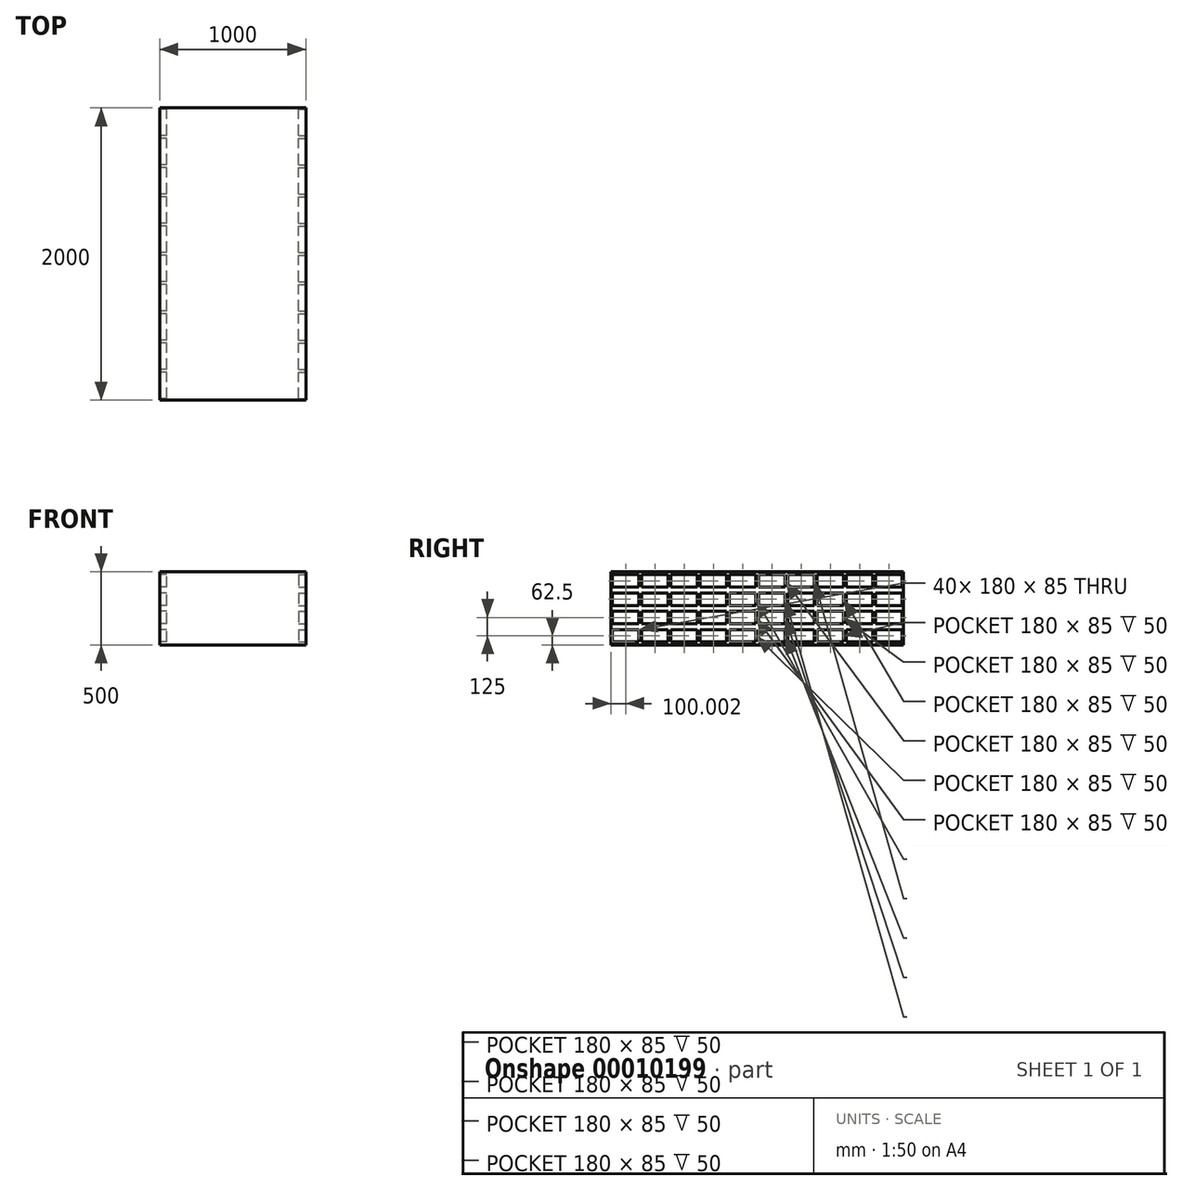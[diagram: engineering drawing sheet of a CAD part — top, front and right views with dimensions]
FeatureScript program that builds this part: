
annotation { "Feature Type Name" : "Feature", "Feature Type Description" : "" }
export const myFeature = defineFeature(function(context is Context, id is Id, definition is map)
    precondition{}
    {
        {
            var Q0;
            Q0=qCreatedBy(makeId("Top.planeOp"),FACE);
            var sketch = newSketch(context, id + "F0", { "sketchPlane" : qUnion([Q0])});
            skLineSegment(sketch, "E0.bottom", {"start": v(-315.45, -1000.92) * mm, "end": v(684.55, -1000.92) * mm});
            skLineSegment(sketch, "E0.top", {"start": v(-315.45, 999.08) * mm, "end": v(684.55, 999.08) * mm});
            skLineSegment(sketch, "E0.left", {"start": v(-315.45, -1000.92) * mm, "end": v(-315.45, 999.08) * mm});
            skLineSegment(sketch, "E0.right", {"start": v(684.55, -1000.92) * mm, "end": v(684.55, 999.08) * mm});
            skSolve(sketch);
        }
        {
            var Q0;
            Q0 = qSketchRegion(id + "F0", true);
            extrude(context, id + "F1", {"entities" : qUnion([Q0]), "depth" : 500 * mm});
        }
        {
            var Q0;
            Q0=makeQuery(id+"F1.opExtrude","SWEPT_FACE",FACE,{"disambiguationData":[OSD([sQuery(id+"F0.wireOp",EDGE,"E0.left")])]});
            var sketch = newSketch(context, id + "F2", { "sketchPlane" : qUnion([Q0])});
            skLineSegment(sketch, "E1.bottom", {"start": v(-809.08, 395) * mm, "end": v(-989.08, 395) * mm});
            skLineSegment(sketch, "E1.top", {"start": v(-809.08, 480) * mm, "end": v(-989.08, 480) * mm});
            skLineSegment(sketch, "E1.left", {"start": v(-809.08, 395) * mm, "end": v(-809.08, 480) * mm});
            skLineSegment(sketch, "E1.right", {"start": v(-989.08, 395) * mm, "end": v(-989.08, 480) * mm});
            skLineSegment(sketch, "E2.0.1.0", {"start": v(-809.08, 270) * mm, "end": v(-989.08, 270) * mm});
            skLineSegment(sketch, "E2.0.1.1", {"start": v(-809.08, 355) * mm, "end": v(-989.08, 355) * mm});
            skLineSegment(sketch, "E2.0.1.2", {"start": v(-809.08, 270) * mm, "end": v(-809.08, 355) * mm});
            skLineSegment(sketch, "E2.0.1.3", {"start": v(-989.08, 270) * mm, "end": v(-989.08, 355) * mm});
            skLineSegment(sketch, "E2.0.2.0", {"start": v(-809.08, 145) * mm, "end": v(-989.08, 145) * mm});
            skLineSegment(sketch, "E2.0.2.1", {"start": v(-809.08, 230) * mm, "end": v(-989.08, 230) * mm});
            skLineSegment(sketch, "E2.0.2.2", {"start": v(-809.08, 145) * mm, "end": v(-809.08, 230) * mm});
            skLineSegment(sketch, "E2.0.2.3", {"start": v(-989.08, 145) * mm, "end": v(-989.08, 230) * mm});
            skLineSegment(sketch, "E2.0.3.0", {"start": v(-809.08, 20) * mm, "end": v(-989.08, 20) * mm});
            skLineSegment(sketch, "E2.0.3.1", {"start": v(-809.08, 105) * mm, "end": v(-989.08, 105) * mm});
            skLineSegment(sketch, "E2.0.3.2", {"start": v(-809.08, 20) * mm, "end": v(-809.08, 105) * mm});
            skLineSegment(sketch, "E2.0.3.3", {"start": v(-989.08, 20) * mm, "end": v(-989.08, 105) * mm});
            skLineSegment(sketch, "E2.1.0.0", {"start": v(-609.08, 395) * mm, "end": v(-789.08, 395) * mm});
            skLineSegment(sketch, "E2.1.0.1", {"start": v(-609.08, 480) * mm, "end": v(-789.08, 480) * mm});
            skLineSegment(sketch, "E2.1.0.2", {"start": v(-609.08, 395) * mm, "end": v(-609.08, 480) * mm});
            skLineSegment(sketch, "E2.1.0.3", {"start": v(-789.08, 395) * mm, "end": v(-789.08, 480) * mm});
            skLineSegment(sketch, "E2.1.1.0", {"start": v(-609.08, 270) * mm, "end": v(-789.08, 270) * mm});
            skLineSegment(sketch, "E2.1.1.1", {"start": v(-609.08, 355) * mm, "end": v(-789.08, 355) * mm});
            skLineSegment(sketch, "E2.1.1.2", {"start": v(-609.08, 270) * mm, "end": v(-609.08, 355) * mm});
            skLineSegment(sketch, "E2.1.1.3", {"start": v(-789.08, 270) * mm, "end": v(-789.08, 355) * mm});
            skLineSegment(sketch, "E2.1.2.0", {"start": v(-609.08, 145) * mm, "end": v(-789.08, 145) * mm});
            skLineSegment(sketch, "E2.1.2.1", {"start": v(-609.08, 230) * mm, "end": v(-789.08, 230) * mm});
            skLineSegment(sketch, "E2.1.2.2", {"start": v(-609.08, 145) * mm, "end": v(-609.08, 230) * mm});
            skLineSegment(sketch, "E2.1.2.3", {"start": v(-789.08, 145) * mm, "end": v(-789.08, 230) * mm});
            skLineSegment(sketch, "E2.1.3.0", {"start": v(-609.08, 20) * mm, "end": v(-789.08, 20) * mm});
            skLineSegment(sketch, "E2.1.3.1", {"start": v(-609.08, 105) * mm, "end": v(-789.08, 105) * mm});
            skLineSegment(sketch, "E2.1.3.2", {"start": v(-609.08, 20) * mm, "end": v(-609.08, 105) * mm});
            skLineSegment(sketch, "E2.1.3.3", {"start": v(-789.08, 20) * mm, "end": v(-789.08, 105) * mm});
            skLineSegment(sketch, "E2.2.0.0", {"start": v(-409.08, 395) * mm, "end": v(-589.08, 395) * mm});
            skLineSegment(sketch, "E2.2.0.1", {"start": v(-409.08, 480) * mm, "end": v(-589.08, 480) * mm});
            skLineSegment(sketch, "E2.2.0.2", {"start": v(-409.08, 395) * mm, "end": v(-409.08, 480) * mm});
            skLineSegment(sketch, "E2.2.0.3", {"start": v(-589.08, 395) * mm, "end": v(-589.08, 480) * mm});
            skLineSegment(sketch, "E2.2.1.0", {"start": v(-409.08, 270) * mm, "end": v(-589.08, 270) * mm});
            skLineSegment(sketch, "E2.2.1.1", {"start": v(-409.08, 355) * mm, "end": v(-589.08, 355) * mm});
            skLineSegment(sketch, "E2.2.1.2", {"start": v(-409.08, 270) * mm, "end": v(-409.08, 355) * mm});
            skLineSegment(sketch, "E2.2.1.3", {"start": v(-589.08, 270) * mm, "end": v(-589.08, 355) * mm});
            skLineSegment(sketch, "E2.2.2.0", {"start": v(-409.08, 145) * mm, "end": v(-589.08, 145) * mm});
            skLineSegment(sketch, "E2.2.2.1", {"start": v(-409.08, 230) * mm, "end": v(-589.08, 230) * mm});
            skLineSegment(sketch, "E2.2.2.2", {"start": v(-409.08, 145) * mm, "end": v(-409.08, 230) * mm});
            skLineSegment(sketch, "E2.2.2.3", {"start": v(-589.08, 145) * mm, "end": v(-589.08, 230) * mm});
            skLineSegment(sketch, "E2.2.3.0", {"start": v(-409.08, 20) * mm, "end": v(-589.08, 20) * mm});
            skLineSegment(sketch, "E2.2.3.1", {"start": v(-409.08, 105) * mm, "end": v(-589.08, 105) * mm});
            skLineSegment(sketch, "E2.2.3.2", {"start": v(-409.08, 20) * mm, "end": v(-409.08, 105) * mm});
            skLineSegment(sketch, "E2.2.3.3", {"start": v(-589.08, 20) * mm, "end": v(-589.08, 105) * mm});
            skLineSegment(sketch, "E2.3.0.0", {"start": v(-209.08, 395) * mm, "end": v(-389.08, 395) * mm});
            skLineSegment(sketch, "E2.3.0.1", {"start": v(-209.08, 480) * mm, "end": v(-389.08, 480) * mm});
            skLineSegment(sketch, "E2.3.0.2", {"start": v(-209.08, 395) * mm, "end": v(-209.08, 480) * mm});
            skLineSegment(sketch, "E2.3.0.3", {"start": v(-389.08, 395) * mm, "end": v(-389.08, 480) * mm});
            skLineSegment(sketch, "E2.3.1.0", {"start": v(-209.08, 270) * mm, "end": v(-389.08, 270) * mm});
            skLineSegment(sketch, "E2.3.1.1", {"start": v(-209.08, 355) * mm, "end": v(-389.08, 355) * mm});
            skLineSegment(sketch, "E2.3.1.2", {"start": v(-209.08, 270) * mm, "end": v(-209.08, 355) * mm});
            skLineSegment(sketch, "E2.3.1.3", {"start": v(-389.08, 270) * mm, "end": v(-389.08, 355) * mm});
            skLineSegment(sketch, "E2.3.2.0", {"start": v(-209.08, 145) * mm, "end": v(-389.08, 145) * mm});
            skLineSegment(sketch, "E2.3.2.1", {"start": v(-209.08, 230) * mm, "end": v(-389.08, 230) * mm});
            skLineSegment(sketch, "E2.3.2.2", {"start": v(-209.08, 145) * mm, "end": v(-209.08, 230) * mm});
            skLineSegment(sketch, "E2.3.2.3", {"start": v(-389.08, 145) * mm, "end": v(-389.08, 230) * mm});
            skLineSegment(sketch, "E2.3.3.0", {"start": v(-209.08, 20) * mm, "end": v(-389.08, 20) * mm});
            skLineSegment(sketch, "E2.3.3.1", {"start": v(-209.08, 105) * mm, "end": v(-389.08, 105) * mm});
            skLineSegment(sketch, "E2.3.3.2", {"start": v(-209.08, 20) * mm, "end": v(-209.08, 105) * mm});
            skLineSegment(sketch, "E2.3.3.3", {"start": v(-389.08, 20) * mm, "end": v(-389.08, 105) * mm});
            skLineSegment(sketch, "E2.4.0.0", {"start": v(-9.08, 395) * mm, "end": v(-189.08, 395) * mm});
            skLineSegment(sketch, "E2.4.0.1", {"start": v(-9.08, 480) * mm, "end": v(-189.08, 480) * mm});
            skLineSegment(sketch, "E2.4.0.2", {"start": v(-9.08, 395) * mm, "end": v(-9.08, 480) * mm});
            skLineSegment(sketch, "E2.4.0.3", {"start": v(-189.08, 395) * mm, "end": v(-189.08, 480) * mm});
            skLineSegment(sketch, "E2.4.1.0", {"start": v(-9.08, 270) * mm, "end": v(-189.08, 270) * mm});
            skLineSegment(sketch, "E2.4.1.1", {"start": v(-9.08, 355) * mm, "end": v(-189.08, 355) * mm});
            skLineSegment(sketch, "E2.4.1.2", {"start": v(-9.08, 270) * mm, "end": v(-9.08, 355) * mm});
            skLineSegment(sketch, "E2.4.1.3", {"start": v(-189.08, 270) * mm, "end": v(-189.08, 355) * mm});
            skLineSegment(sketch, "E2.4.2.0", {"start": v(-9.08, 145) * mm, "end": v(-189.08, 145) * mm});
            skLineSegment(sketch, "E2.4.2.1", {"start": v(-9.08, 230) * mm, "end": v(-189.08, 230) * mm});
            skLineSegment(sketch, "E2.4.2.2", {"start": v(-9.08, 145) * mm, "end": v(-9.08, 230) * mm});
            skLineSegment(sketch, "E2.4.2.3", {"start": v(-189.08, 145) * mm, "end": v(-189.08, 230) * mm});
            skLineSegment(sketch, "E2.4.3.0", {"start": v(-9.08, 20) * mm, "end": v(-189.08, 20) * mm});
            skLineSegment(sketch, "E2.4.3.1", {"start": v(-9.08, 105) * mm, "end": v(-189.08, 105) * mm});
            skLineSegment(sketch, "E2.4.3.2", {"start": v(-9.08, 20) * mm, "end": v(-9.08, 105) * mm});
            skLineSegment(sketch, "E2.4.3.3", {"start": v(-189.08, 20) * mm, "end": v(-189.08, 105) * mm});
            skLineSegment(sketch, "E2.5.0.0", {"start": v(190.92, 395) * mm, "end": v(10.92, 395) * mm});
            skLineSegment(sketch, "E2.5.0.1", {"start": v(190.92, 480) * mm, "end": v(10.92, 480) * mm});
            skLineSegment(sketch, "E2.5.0.2", {"start": v(190.92, 395) * mm, "end": v(190.92, 480) * mm});
            skLineSegment(sketch, "E2.5.0.3", {"start": v(10.92, 395) * mm, "end": v(10.92, 480) * mm});
            skLineSegment(sketch, "E2.5.1.0", {"start": v(190.92, 270) * mm, "end": v(10.92, 270) * mm});
            skLineSegment(sketch, "E2.5.1.1", {"start": v(190.92, 355) * mm, "end": v(10.92, 355) * mm});
            skLineSegment(sketch, "E2.5.1.2", {"start": v(190.92, 270) * mm, "end": v(190.92, 355) * mm});
            skLineSegment(sketch, "E2.5.1.3", {"start": v(10.92, 270) * mm, "end": v(10.92, 355) * mm});
            skLineSegment(sketch, "E2.5.2.0", {"start": v(190.92, 145) * mm, "end": v(10.92, 145) * mm});
            skLineSegment(sketch, "E2.5.2.1", {"start": v(190.92, 230) * mm, "end": v(10.92, 230) * mm});
            skLineSegment(sketch, "E2.5.2.2", {"start": v(190.92, 145) * mm, "end": v(190.92, 230) * mm});
            skLineSegment(sketch, "E2.5.2.3", {"start": v(10.92, 145) * mm, "end": v(10.92, 230) * mm});
            skLineSegment(sketch, "E2.5.3.0", {"start": v(190.92, 20) * mm, "end": v(10.92, 20) * mm});
            skLineSegment(sketch, "E2.5.3.1", {"start": v(190.92, 105) * mm, "end": v(10.92, 105) * mm});
            skLineSegment(sketch, "E2.5.3.2", {"start": v(190.92, 20) * mm, "end": v(190.92, 105) * mm});
            skLineSegment(sketch, "E2.5.3.3", {"start": v(10.92, 20) * mm, "end": v(10.92, 105) * mm});
            skLineSegment(sketch, "E2.6.0.0", {"start": v(390.92, 395) * mm, "end": v(210.92, 395) * mm});
            skLineSegment(sketch, "E2.6.0.1", {"start": v(390.92, 480) * mm, "end": v(210.92, 480) * mm});
            skLineSegment(sketch, "E2.6.0.2", {"start": v(390.92, 395) * mm, "end": v(390.92, 480) * mm});
            skLineSegment(sketch, "E2.6.0.3", {"start": v(210.92, 395) * mm, "end": v(210.92, 480) * mm});
            skLineSegment(sketch, "E2.6.1.0", {"start": v(390.92, 270) * mm, "end": v(210.92, 270) * mm});
            skLineSegment(sketch, "E2.6.1.1", {"start": v(390.92, 355) * mm, "end": v(210.92, 355) * mm});
            skLineSegment(sketch, "E2.6.1.2", {"start": v(390.92, 270) * mm, "end": v(390.92, 355) * mm});
            skLineSegment(sketch, "E2.6.1.3", {"start": v(210.92, 270) * mm, "end": v(210.92, 355) * mm});
            skLineSegment(sketch, "E2.6.2.0", {"start": v(390.92, 145) * mm, "end": v(210.92, 145) * mm});
            skLineSegment(sketch, "E2.6.2.1", {"start": v(390.92, 230) * mm, "end": v(210.92, 230) * mm});
            skLineSegment(sketch, "E2.6.2.2", {"start": v(390.92, 145) * mm, "end": v(390.92, 230) * mm});
            skLineSegment(sketch, "E2.6.2.3", {"start": v(210.92, 145) * mm, "end": v(210.92, 230) * mm});
            skLineSegment(sketch, "E2.6.3.0", {"start": v(390.92, 20) * mm, "end": v(210.92, 20) * mm});
            skLineSegment(sketch, "E2.6.3.1", {"start": v(390.92, 105) * mm, "end": v(210.92, 105) * mm});
            skLineSegment(sketch, "E2.6.3.2", {"start": v(390.92, 20) * mm, "end": v(390.92, 105) * mm});
            skLineSegment(sketch, "E2.6.3.3", {"start": v(210.92, 20) * mm, "end": v(210.92, 105) * mm});
            skLineSegment(sketch, "E2.7.0.0", {"start": v(590.92, 395) * mm, "end": v(410.92, 395) * mm});
            skLineSegment(sketch, "E2.7.0.1", {"start": v(590.92, 480) * mm, "end": v(410.92, 480) * mm});
            skLineSegment(sketch, "E2.7.0.2", {"start": v(590.92, 395) * mm, "end": v(590.92, 480) * mm});
            skLineSegment(sketch, "E2.7.0.3", {"start": v(410.92, 395) * mm, "end": v(410.92, 480) * mm});
            skLineSegment(sketch, "E2.7.1.0", {"start": v(590.92, 270) * mm, "end": v(410.92, 270) * mm});
            skLineSegment(sketch, "E2.7.1.1", {"start": v(590.92, 355) * mm, "end": v(410.92, 355) * mm});
            skLineSegment(sketch, "E2.7.1.2", {"start": v(590.92, 270) * mm, "end": v(590.92, 355) * mm});
            skLineSegment(sketch, "E2.7.1.3", {"start": v(410.92, 270) * mm, "end": v(410.92, 355) * mm});
            skLineSegment(sketch, "E2.7.2.0", {"start": v(590.92, 145) * mm, "end": v(410.92, 145) * mm});
            skLineSegment(sketch, "E2.7.2.1", {"start": v(590.92, 230) * mm, "end": v(410.92, 230) * mm});
            skLineSegment(sketch, "E2.7.2.2", {"start": v(590.92, 145) * mm, "end": v(590.92, 230) * mm});
            skLineSegment(sketch, "E2.7.2.3", {"start": v(410.92, 145) * mm, "end": v(410.92, 230) * mm});
            skLineSegment(sketch, "E2.7.3.0", {"start": v(590.92, 20) * mm, "end": v(410.92, 20) * mm});
            skLineSegment(sketch, "E2.7.3.1", {"start": v(590.92, 105) * mm, "end": v(410.92, 105) * mm});
            skLineSegment(sketch, "E2.7.3.2", {"start": v(590.92, 20) * mm, "end": v(590.92, 105) * mm});
            skLineSegment(sketch, "E2.7.3.3", {"start": v(410.92, 20) * mm, "end": v(410.92, 105) * mm});
            skLineSegment(sketch, "E2.8.0.0", {"start": v(790.92, 395) * mm, "end": v(610.92, 395) * mm});
            skLineSegment(sketch, "E2.8.0.1", {"start": v(790.92, 480) * mm, "end": v(610.92, 480) * mm});
            skLineSegment(sketch, "E2.8.0.2", {"start": v(790.92, 395) * mm, "end": v(790.92, 480) * mm});
            skLineSegment(sketch, "E2.8.0.3", {"start": v(610.92, 395) * mm, "end": v(610.92, 480) * mm});
            skLineSegment(sketch, "E2.8.1.0", {"start": v(790.92, 270) * mm, "end": v(610.92, 270) * mm});
            skLineSegment(sketch, "E2.8.1.1", {"start": v(790.92, 355) * mm, "end": v(610.92, 355) * mm});
            skLineSegment(sketch, "E2.8.1.2", {"start": v(790.92, 270) * mm, "end": v(790.92, 355) * mm});
            skLineSegment(sketch, "E2.8.1.3", {"start": v(610.92, 270) * mm, "end": v(610.92, 355) * mm});
            skLineSegment(sketch, "E2.8.2.0", {"start": v(790.92, 145) * mm, "end": v(610.92, 145) * mm});
            skLineSegment(sketch, "E2.8.2.1", {"start": v(790.92, 230) * mm, "end": v(610.92, 230) * mm});
            skLineSegment(sketch, "E2.8.2.2", {"start": v(790.92, 145) * mm, "end": v(790.92, 230) * mm});
            skLineSegment(sketch, "E2.8.2.3", {"start": v(610.92, 145) * mm, "end": v(610.92, 230) * mm});
            skLineSegment(sketch, "E2.8.3.0", {"start": v(790.92, 20) * mm, "end": v(610.92, 20) * mm});
            skLineSegment(sketch, "E2.8.3.1", {"start": v(790.92, 105) * mm, "end": v(610.92, 105) * mm});
            skLineSegment(sketch, "E2.8.3.2", {"start": v(790.92, 20) * mm, "end": v(790.92, 105) * mm});
            skLineSegment(sketch, "E2.8.3.3", {"start": v(610.92, 20) * mm, "end": v(610.92, 105) * mm});
            skLineSegment(sketch, "E2.9.0.0", {"start": v(990.92, 395) * mm, "end": v(810.92, 395) * mm});
            skLineSegment(sketch, "E2.9.0.1", {"start": v(990.92, 480) * mm, "end": v(810.92, 480) * mm});
            skLineSegment(sketch, "E2.9.0.2", {"start": v(990.92, 395) * mm, "end": v(990.92, 480) * mm});
            skLineSegment(sketch, "E2.9.0.3", {"start": v(810.92, 395) * mm, "end": v(810.92, 480) * mm});
            skLineSegment(sketch, "E2.9.1.0", {"start": v(990.92, 270) * mm, "end": v(810.92, 270) * mm});
            skLineSegment(sketch, "E2.9.1.1", {"start": v(990.92, 355) * mm, "end": v(810.92, 355) * mm});
            skLineSegment(sketch, "E2.9.1.2", {"start": v(990.92, 270) * mm, "end": v(990.92, 355) * mm});
            skLineSegment(sketch, "E2.9.1.3", {"start": v(810.92, 270) * mm, "end": v(810.92, 355) * mm});
            skLineSegment(sketch, "E2.9.2.0", {"start": v(990.92, 145) * mm, "end": v(810.92, 145) * mm});
            skLineSegment(sketch, "E2.9.2.1", {"start": v(990.92, 230) * mm, "end": v(810.92, 230) * mm});
            skLineSegment(sketch, "E2.9.2.2", {"start": v(990.92, 145) * mm, "end": v(990.92, 230) * mm});
            skLineSegment(sketch, "E2.9.2.3", {"start": v(810.92, 145) * mm, "end": v(810.92, 230) * mm});
            skLineSegment(sketch, "E2.9.3.0", {"start": v(990.92, 20) * mm, "end": v(810.92, 20) * mm});
            skLineSegment(sketch, "E2.9.3.1", {"start": v(990.92, 105) * mm, "end": v(810.92, 105) * mm});
            skLineSegment(sketch, "E2.9.3.2", {"start": v(990.92, 20) * mm, "end": v(990.92, 105) * mm});
            skLineSegment(sketch, "E2.9.3.3", {"start": v(810.92, 20) * mm, "end": v(810.92, 105) * mm});
            skLineSegment(sketch, "E2.direction1", {"start": v(-989.08, 395) * mm, "end": v(-789.08, 395) * mm, "construction": true});
            skLineSegment(sketch, "E2.direction2", {"start": v(-989.08, 395) * mm, "end": v(-989.08, 270) * mm, "construction": true});
            skSolve(sketch);
        }
        {
            var Q0;
            Q0=makeQuery(id+"F2.imprint","IMPRINT",FACE,{"disambiguationData":[TD([[makeQuery(id+"F2.imprint","IMPRINT",EDGE,{"derivedFrom":sQuery(id+"F2.wireOp",EDGE,"E2.0.3.0")}),-1.0]])]});
            var Q1;
            Q1=makeQuery(id+"F2.imprint","IMPRINT",FACE,{"disambiguationData":[TD([[makeQuery(id+"F2.imprint","IMPRINT",EDGE,{"derivedFrom":sQuery(id+"F2.wireOp",EDGE,"E2.9.0.0")}),-1.0]])]});
            var Q2;
            Q2=makeQuery(id+"F2.imprint","IMPRINT",FACE,{"disambiguationData":[TD([[makeQuery(id+"F2.imprint","IMPRINT",EDGE,{"derivedFrom":sQuery(id+"F2.wireOp",EDGE,"E2.0.2.0")}),-1.0]])]});
            var Q3;
            Q3=makeQuery(id+"F2.imprint","IMPRINT",FACE,{"disambiguationData":[TD([[makeQuery(id+"F2.imprint","IMPRINT",EDGE,{"derivedFrom":sQuery(id+"F2.wireOp",EDGE,"E2.0.1.0")}),-1.0]])]});
            var Q4;
            Q4=makeQuery(id+"F2.imprint","IMPRINT",FACE,{"disambiguationData":[TD([[makeQuery(id+"F2.imprint","IMPRINT",EDGE,{"derivedFrom":sQuery(id+"F2.wireOp",EDGE,"E2.1.3.0")}),-1.0]])]});
            var Q5;
            Q5=makeQuery(id+"F2.imprint","IMPRINT",FACE,{"disambiguationData":[TD([[makeQuery(id+"F2.imprint","IMPRINT",EDGE,{"derivedFrom":sQuery(id+"F2.wireOp",EDGE,"E2.2.2.0")}),-1.0]])]});
            var Q6;
            Q6=makeQuery(id+"F2.imprint","IMPRINT",FACE,{"disambiguationData":[TD([[makeQuery(id+"F2.imprint","IMPRINT",EDGE,{"derivedFrom":sQuery(id+"F2.wireOp",EDGE,"E2.2.3.0")}),-1.0]])]});
            var Q7;
            Q7=makeQuery(id+"F2.imprint","IMPRINT",FACE,{"disambiguationData":[TD([[makeQuery(id+"F2.imprint","IMPRINT",EDGE,{"derivedFrom":sQuery(id+"F2.wireOp",EDGE,"E2.6.3.0")}),-1.0]])]});
            var Q8;
            Q8=makeQuery(id+"F2.imprint","IMPRINT",FACE,{"disambiguationData":[TD([[makeQuery(id+"F2.imprint","IMPRINT",EDGE,{"derivedFrom":sQuery(id+"F2.wireOp",EDGE,"E2.5.0.0")}),-1.0]])]});
            var Q9;
            Q9=makeQuery(id+"F2.imprint","IMPRINT",FACE,{"disambiguationData":[TD([[makeQuery(id+"F2.imprint","IMPRINT",EDGE,{"derivedFrom":sQuery(id+"F2.wireOp",EDGE,"E2.8.3.0")}),-1.0]])]});
            var Q10;
            Q10=makeQuery(id+"F2.imprint","IMPRINT",FACE,{"disambiguationData":[TD([[makeQuery(id+"F2.imprint","IMPRINT",EDGE,{"derivedFrom":sQuery(id+"F2.wireOp",EDGE,"E2.4.3.0")}),-1.0]])]});
            var Q11;
            Q11=makeQuery(id+"F2.imprint","IMPRINT",FACE,{"disambiguationData":[TD([[makeQuery(id+"F2.imprint","IMPRINT",EDGE,{"derivedFrom":sQuery(id+"F2.wireOp",EDGE,"E2.3.3.0")}),-1.0]])]});
            var Q12;
            Q12=makeQuery(id+"F2.imprint","IMPRINT",FACE,{"disambiguationData":[TD([[makeQuery(id+"F2.imprint","IMPRINT",EDGE,{"derivedFrom":sQuery(id+"F2.wireOp",EDGE,"E1.bottom")}),-1.0]])]});
            var Q13;
            Q13=makeQuery(id+"F2.imprint","IMPRINT",FACE,{"disambiguationData":[TD([[makeQuery(id+"F2.imprint","IMPRINT",EDGE,{"derivedFrom":sQuery(id+"F2.wireOp",EDGE,"E2.3.2.0")}),-1.0]])]});
            var Q14;
            Q14=makeQuery(id+"F2.imprint","IMPRINT",FACE,{"disambiguationData":[TD([[makeQuery(id+"F2.imprint","IMPRINT",EDGE,{"derivedFrom":sQuery(id+"F2.wireOp",EDGE,"E2.1.1.0")}),-1.0]])]});
            var Q15;
            Q15=makeQuery(id+"F2.imprint","IMPRINT",FACE,{"disambiguationData":[TD([[makeQuery(id+"F2.imprint","IMPRINT",EDGE,{"derivedFrom":sQuery(id+"F2.wireOp",EDGE,"E2.1.2.0")}),-1.0]])]});
            var Q16;
            Q16=makeQuery(id+"F2.imprint","IMPRINT",FACE,{"disambiguationData":[TD([[makeQuery(id+"F2.imprint","IMPRINT",EDGE,{"derivedFrom":sQuery(id+"F2.wireOp",EDGE,"E2.2.1.0")}),-1.0]])]});
            var Q17;
            Q17=makeQuery(id+"F2.imprint","IMPRINT",FACE,{"disambiguationData":[TD([[makeQuery(id+"F2.imprint","IMPRINT",EDGE,{"derivedFrom":sQuery(id+"F2.wireOp",EDGE,"E2.3.0.0")}),-1.0]])]});
            var Q18;
            Q18=makeQuery(id+"F2.imprint","IMPRINT",FACE,{"disambiguationData":[TD([[makeQuery(id+"F2.imprint","IMPRINT",EDGE,{"derivedFrom":sQuery(id+"F2.wireOp",EDGE,"E2.9.2.0")}),-1.0]])]});
            var Q19;
            Q19=makeQuery(id+"F2.imprint","IMPRINT",FACE,{"disambiguationData":[TD([[makeQuery(id+"F2.imprint","IMPRINT",EDGE,{"derivedFrom":sQuery(id+"F2.wireOp",EDGE,"E2.9.1.0")}),-1.0]])]});
            var Q20;
            Q20=makeQuery(id+"F2.imprint","IMPRINT",FACE,{"disambiguationData":[TD([[makeQuery(id+"F2.imprint","IMPRINT",EDGE,{"derivedFrom":sQuery(id+"F2.wireOp",EDGE,"E2.7.0.0")}),-1.0]])]});
            var Q21;
            Q21=makeQuery(id+"F2.imprint","IMPRINT",FACE,{"disambiguationData":[TD([[makeQuery(id+"F2.imprint","IMPRINT",EDGE,{"derivedFrom":sQuery(id+"F2.wireOp",EDGE,"E2.7.3.0")}),-1.0]])]});
            var Q22;
            Q22=makeQuery(id+"F2.imprint","IMPRINT",FACE,{"disambiguationData":[TD([[makeQuery(id+"F2.imprint","IMPRINT",EDGE,{"derivedFrom":sQuery(id+"F2.wireOp",EDGE,"E2.7.1.0")}),-1.0]])]});
            var Q23;
            Q23=makeQuery(id+"F2.imprint","IMPRINT",FACE,{"disambiguationData":[TD([[makeQuery(id+"F2.imprint","IMPRINT",EDGE,{"derivedFrom":sQuery(id+"F2.wireOp",EDGE,"E2.3.1.0")}),-1.0]])]});
            var Q24;
            Q24=makeQuery(id+"F2.imprint","IMPRINT",FACE,{"disambiguationData":[TD([[makeQuery(id+"F2.imprint","IMPRINT",EDGE,{"derivedFrom":sQuery(id+"F2.wireOp",EDGE,"E2.4.2.0")}),-1.0]])]});
            var Q25;
            Q25=makeQuery(id+"F2.imprint","IMPRINT",FACE,{"disambiguationData":[TD([[makeQuery(id+"F2.imprint","IMPRINT",EDGE,{"derivedFrom":sQuery(id+"F2.wireOp",EDGE,"E2.1.0.0")}),-1.0]])]});
            var Q26;
            Q26=makeQuery(id+"F2.imprint","IMPRINT",FACE,{"disambiguationData":[TD([[makeQuery(id+"F2.imprint","IMPRINT",EDGE,{"derivedFrom":sQuery(id+"F2.wireOp",EDGE,"E2.8.1.0")}),-1.0]])]});
            var Q27;
            Q27=makeQuery(id+"F2.imprint","IMPRINT",FACE,{"disambiguationData":[TD([[makeQuery(id+"F2.imprint","IMPRINT",EDGE,{"derivedFrom":sQuery(id+"F2.wireOp",EDGE,"E2.4.0.0")}),-1.0]])]});
            var Q28;
            Q28=makeQuery(id+"F2.imprint","IMPRINT",FACE,{"disambiguationData":[TD([[makeQuery(id+"F2.imprint","IMPRINT",EDGE,{"derivedFrom":sQuery(id+"F2.wireOp",EDGE,"E2.8.0.0")}),-1.0]])]});
            var Q29;
            Q29=makeQuery(id+"F2.imprint","IMPRINT",FACE,{"disambiguationData":[TD([[makeQuery(id+"F2.imprint","IMPRINT",EDGE,{"derivedFrom":sQuery(id+"F2.wireOp",EDGE,"E2.6.0.0")}),-1.0]])]});
            var Q30;
            Q30=makeQuery(id+"F2.imprint","IMPRINT",FACE,{"disambiguationData":[TD([[makeQuery(id+"F2.imprint","IMPRINT",EDGE,{"derivedFrom":sQuery(id+"F2.wireOp",EDGE,"E2.5.3.0")}),-1.0]])]});
            var Q31;
            Q31=makeQuery(id+"F2.imprint","IMPRINT",FACE,{"disambiguationData":[TD([[makeQuery(id+"F2.imprint","IMPRINT",EDGE,{"derivedFrom":sQuery(id+"F2.wireOp",EDGE,"E2.9.3.0")}),-1.0]])]});
            var Q32;
            Q32=makeQuery(id+"F2.imprint","IMPRINT",FACE,{"disambiguationData":[TD([[makeQuery(id+"F2.imprint","IMPRINT",EDGE,{"derivedFrom":sQuery(id+"F2.wireOp",EDGE,"E2.5.1.0")}),-1.0]])]});
            var Q33;
            Q33=makeQuery(id+"F2.imprint","IMPRINT",FACE,{"disambiguationData":[TD([[makeQuery(id+"F2.imprint","IMPRINT",EDGE,{"derivedFrom":sQuery(id+"F2.wireOp",EDGE,"E2.4.1.0")}),-1.0]])]});
            var Q34;
            Q34=makeQuery(id+"F2.imprint","IMPRINT",FACE,{"disambiguationData":[TD([[makeQuery(id+"F2.imprint","IMPRINT",EDGE,{"derivedFrom":sQuery(id+"F2.wireOp",EDGE,"E2.2.0.0")}),-1.0]])]});
            var Q35;
            Q35=makeQuery(id+"F2.imprint","IMPRINT",FACE,{"disambiguationData":[TD([[makeQuery(id+"F2.imprint","IMPRINT",EDGE,{"derivedFrom":sQuery(id+"F2.wireOp",EDGE,"E2.6.2.0")}),-1.0]])]});
            var Q36;
            Q36=makeQuery(id+"F2.imprint","IMPRINT",FACE,{"disambiguationData":[TD([[makeQuery(id+"F2.imprint","IMPRINT",EDGE,{"derivedFrom":sQuery(id+"F2.wireOp",EDGE,"E2.6.1.0")}),-1.0]])]});
            var Q37;
            Q37=makeQuery(id+"F2.imprint","IMPRINT",FACE,{"disambiguationData":[TD([[makeQuery(id+"F2.imprint","IMPRINT",EDGE,{"derivedFrom":sQuery(id+"F2.wireOp",EDGE,"E2.5.2.0")}),-1.0]])]});
            var Q38;
            Q38=makeQuery(id+"F2.imprint","IMPRINT",FACE,{"disambiguationData":[TD([[makeQuery(id+"F2.imprint","IMPRINT",EDGE,{"derivedFrom":sQuery(id+"F2.wireOp",EDGE,"E2.7.2.0")}),-1.0]])]});
            var Q39;
            Q39=makeQuery(id+"F2.imprint","IMPRINT",FACE,{"disambiguationData":[TD([[makeQuery(id+"F2.imprint","IMPRINT",EDGE,{"derivedFrom":sQuery(id+"F2.wireOp",EDGE,"E2.8.2.0")}),-1.0]])]});
            extrude(context, id + "F3", {"entities" : qUnion([Q0, Q1, Q2, Q3, Q4, Q5, Q6, Q7, Q8, Q9, Q10, Q11, Q12, Q13, Q14, Q15, Q16, Q17, Q18, Q19, Q20, Q21, Q22, Q23, Q24, Q25, Q26, Q27, Q28, Q29, Q30, Q31, Q32, Q33, Q34, Q35, Q36, Q37, Q38, Q39]), "operationType" : NewBodyOperationType.REMOVE, "oppositeDirection" : true, "depth" : 50 * mm});
        }
        {
            var Q0;
            Q0=makeQuery(id+"F1.opExtrude","SWEPT_FACE",FACE,{"disambiguationData":[OSD([sQuery(id+"F0.wireOp",EDGE,"E0.right")])]});
            var sketch = newSketch(context, id + "F4", { "sketchPlane" : qUnion([Q0])});
            skLineSegment(sketch, "E3.bottom", {"start": v(-990.92, 480) * mm, "end": v(-810.92, 480) * mm});
            skLineSegment(sketch, "E3.top", {"start": v(-990.92, 395) * mm, "end": v(-810.92, 395) * mm});
            skLineSegment(sketch, "E3.left", {"start": v(-990.92, 480) * mm, "end": v(-990.92, 395) * mm});
            skLineSegment(sketch, "E3.right", {"start": v(-810.92, 480) * mm, "end": v(-810.92, 395) * mm});
            skLineSegment(sketch, "E4.0.1.0", {"start": v(-990.92, 270) * mm, "end": v(-810.92, 270) * mm});
            skLineSegment(sketch, "E4.0.1.1", {"start": v(-990.92, 355) * mm, "end": v(-990.92, 270) * mm});
            skLineSegment(sketch, "E4.0.1.2", {"start": v(-990.92, 355) * mm, "end": v(-810.92, 355) * mm});
            skLineSegment(sketch, "E4.0.1.3", {"start": v(-810.92, 355) * mm, "end": v(-810.92, 270) * mm});
            skLineSegment(sketch, "E4.0.2.0", {"start": v(-990.92, 145) * mm, "end": v(-810.92, 145) * mm});
            skLineSegment(sketch, "E4.0.2.1", {"start": v(-990.92, 230) * mm, "end": v(-990.92, 145) * mm});
            skLineSegment(sketch, "E4.0.2.2", {"start": v(-990.92, 230) * mm, "end": v(-810.92, 230) * mm});
            skLineSegment(sketch, "E4.0.2.3", {"start": v(-810.92, 230) * mm, "end": v(-810.92, 145) * mm});
            skLineSegment(sketch, "E4.0.3.0", {"start": v(-990.92, 20) * mm, "end": v(-810.92, 20) * mm});
            skLineSegment(sketch, "E4.0.3.1", {"start": v(-990.92, 105) * mm, "end": v(-990.92, 20) * mm});
            skLineSegment(sketch, "E4.0.3.2", {"start": v(-990.92, 105) * mm, "end": v(-810.92, 105) * mm});
            skLineSegment(sketch, "E4.0.3.3", {"start": v(-810.92, 105) * mm, "end": v(-810.92, 20) * mm});
            skLineSegment(sketch, "E4.1.0.0", {"start": v(-790.92, 395) * mm, "end": v(-610.92, 395) * mm});
            skLineSegment(sketch, "E4.1.0.1", {"start": v(-790.92, 480) * mm, "end": v(-790.92, 395) * mm});
            skLineSegment(sketch, "E4.1.0.2", {"start": v(-790.92, 480) * mm, "end": v(-610.92, 480) * mm});
            skLineSegment(sketch, "E4.1.0.3", {"start": v(-610.92, 480) * mm, "end": v(-610.92, 395) * mm});
            skLineSegment(sketch, "E4.1.1.0", {"start": v(-790.92, 270) * mm, "end": v(-610.92, 270) * mm});
            skLineSegment(sketch, "E4.1.1.1", {"start": v(-790.92, 355) * mm, "end": v(-790.92, 270) * mm});
            skLineSegment(sketch, "E4.1.1.2", {"start": v(-790.92, 355) * mm, "end": v(-610.92, 355) * mm});
            skLineSegment(sketch, "E4.1.1.3", {"start": v(-610.92, 355) * mm, "end": v(-610.92, 270) * mm});
            skLineSegment(sketch, "E4.1.2.0", {"start": v(-790.92, 145) * mm, "end": v(-610.92, 145) * mm});
            skLineSegment(sketch, "E4.1.2.1", {"start": v(-790.92, 230) * mm, "end": v(-790.92, 145) * mm});
            skLineSegment(sketch, "E4.1.2.2", {"start": v(-790.92, 230) * mm, "end": v(-610.92, 230) * mm});
            skLineSegment(sketch, "E4.1.2.3", {"start": v(-610.92, 230) * mm, "end": v(-610.92, 145) * mm});
            skLineSegment(sketch, "E4.1.3.0", {"start": v(-790.92, 20) * mm, "end": v(-610.92, 20) * mm});
            skLineSegment(sketch, "E4.1.3.1", {"start": v(-790.92, 105) * mm, "end": v(-790.92, 20) * mm});
            skLineSegment(sketch, "E4.1.3.2", {"start": v(-790.92, 105) * mm, "end": v(-610.92, 105) * mm});
            skLineSegment(sketch, "E4.1.3.3", {"start": v(-610.92, 105) * mm, "end": v(-610.92, 20) * mm});
            skLineSegment(sketch, "E4.2.0.0", {"start": v(-590.92, 395) * mm, "end": v(-410.92, 395) * mm});
            skLineSegment(sketch, "E4.2.0.1", {"start": v(-590.92, 480) * mm, "end": v(-590.92, 395) * mm});
            skLineSegment(sketch, "E4.2.0.2", {"start": v(-590.92, 480) * mm, "end": v(-410.92, 480) * mm});
            skLineSegment(sketch, "E4.2.0.3", {"start": v(-410.92, 480) * mm, "end": v(-410.92, 395) * mm});
            skLineSegment(sketch, "E4.2.1.0", {"start": v(-590.92, 270) * mm, "end": v(-410.92, 270) * mm});
            skLineSegment(sketch, "E4.2.1.1", {"start": v(-590.92, 355) * mm, "end": v(-590.92, 270) * mm});
            skLineSegment(sketch, "E4.2.1.2", {"start": v(-590.92, 355) * mm, "end": v(-410.92, 355) * mm});
            skLineSegment(sketch, "E4.2.1.3", {"start": v(-410.92, 355) * mm, "end": v(-410.92, 270) * mm});
            skLineSegment(sketch, "E4.2.2.0", {"start": v(-590.92, 145) * mm, "end": v(-410.92, 145) * mm});
            skLineSegment(sketch, "E4.2.2.1", {"start": v(-590.92, 230) * mm, "end": v(-590.92, 145) * mm});
            skLineSegment(sketch, "E4.2.2.2", {"start": v(-590.92, 230) * mm, "end": v(-410.92, 230) * mm});
            skLineSegment(sketch, "E4.2.2.3", {"start": v(-410.92, 230) * mm, "end": v(-410.92, 145) * mm});
            skLineSegment(sketch, "E4.2.3.0", {"start": v(-590.92, 20) * mm, "end": v(-410.92, 20) * mm});
            skLineSegment(sketch, "E4.2.3.1", {"start": v(-590.92, 105) * mm, "end": v(-590.92, 20) * mm});
            skLineSegment(sketch, "E4.2.3.2", {"start": v(-590.92, 105) * mm, "end": v(-410.92, 105) * mm});
            skLineSegment(sketch, "E4.2.3.3", {"start": v(-410.92, 105) * mm, "end": v(-410.92, 20) * mm});
            skLineSegment(sketch, "E4.3.0.0", {"start": v(-390.92, 395) * mm, "end": v(-210.92, 395) * mm});
            skLineSegment(sketch, "E4.3.0.1", {"start": v(-390.92, 480) * mm, "end": v(-390.92, 395) * mm});
            skLineSegment(sketch, "E4.3.0.2", {"start": v(-390.92, 480) * mm, "end": v(-210.92, 480) * mm});
            skLineSegment(sketch, "E4.3.0.3", {"start": v(-210.92, 480) * mm, "end": v(-210.92, 395) * mm});
            skLineSegment(sketch, "E4.3.1.0", {"start": v(-390.92, 270) * mm, "end": v(-210.92, 270) * mm});
            skLineSegment(sketch, "E4.3.1.1", {"start": v(-390.92, 355) * mm, "end": v(-390.92, 270) * mm});
            skLineSegment(sketch, "E4.3.1.2", {"start": v(-390.92, 355) * mm, "end": v(-210.92, 355) * mm});
            skLineSegment(sketch, "E4.3.1.3", {"start": v(-210.92, 355) * mm, "end": v(-210.92, 270) * mm});
            skLineSegment(sketch, "E4.3.2.0", {"start": v(-390.92, 145) * mm, "end": v(-210.92, 145) * mm});
            skLineSegment(sketch, "E4.3.2.1", {"start": v(-390.92, 230) * mm, "end": v(-390.92, 145) * mm});
            skLineSegment(sketch, "E4.3.2.2", {"start": v(-390.92, 230) * mm, "end": v(-210.92, 230) * mm});
            skLineSegment(sketch, "E4.3.2.3", {"start": v(-210.92, 230) * mm, "end": v(-210.92, 145) * mm});
            skLineSegment(sketch, "E4.3.3.0", {"start": v(-390.92, 20) * mm, "end": v(-210.92, 20) * mm});
            skLineSegment(sketch, "E4.3.3.1", {"start": v(-390.92, 105) * mm, "end": v(-390.92, 20) * mm});
            skLineSegment(sketch, "E4.3.3.2", {"start": v(-390.92, 105) * mm, "end": v(-210.92, 105) * mm});
            skLineSegment(sketch, "E4.3.3.3", {"start": v(-210.92, 105) * mm, "end": v(-210.92, 20) * mm});
            skLineSegment(sketch, "E4.4.0.0", {"start": v(-190.92, 395) * mm, "end": v(-10.92, 395) * mm});
            skLineSegment(sketch, "E4.4.0.1", {"start": v(-190.92, 480) * mm, "end": v(-190.92, 395) * mm});
            skLineSegment(sketch, "E4.4.0.2", {"start": v(-190.92, 480) * mm, "end": v(-10.92, 480) * mm});
            skLineSegment(sketch, "E4.4.0.3", {"start": v(-10.92, 480) * mm, "end": v(-10.92, 395) * mm});
            skLineSegment(sketch, "E4.4.1.0", {"start": v(-190.92, 270) * mm, "end": v(-10.92, 270) * mm});
            skLineSegment(sketch, "E4.4.1.1", {"start": v(-190.92, 355) * mm, "end": v(-190.92, 270) * mm});
            skLineSegment(sketch, "E4.4.1.2", {"start": v(-190.92, 355) * mm, "end": v(-10.92, 355) * mm});
            skLineSegment(sketch, "E4.4.1.3", {"start": v(-10.92, 355) * mm, "end": v(-10.92, 270) * mm});
            skLineSegment(sketch, "E4.4.2.0", {"start": v(-190.92, 145) * mm, "end": v(-10.92, 145) * mm});
            skLineSegment(sketch, "E4.4.2.1", {"start": v(-190.92, 230) * mm, "end": v(-190.92, 145) * mm});
            skLineSegment(sketch, "E4.4.2.2", {"start": v(-190.92, 230) * mm, "end": v(-10.92, 230) * mm});
            skLineSegment(sketch, "E4.4.2.3", {"start": v(-10.92, 230) * mm, "end": v(-10.92, 145) * mm});
            skLineSegment(sketch, "E4.4.3.0", {"start": v(-190.92, 20) * mm, "end": v(-10.92, 20) * mm});
            skLineSegment(sketch, "E4.4.3.1", {"start": v(-190.92, 105) * mm, "end": v(-190.92, 20) * mm});
            skLineSegment(sketch, "E4.4.3.2", {"start": v(-190.92, 105) * mm, "end": v(-10.92, 105) * mm});
            skLineSegment(sketch, "E4.4.3.3", {"start": v(-10.92, 105) * mm, "end": v(-10.92, 20) * mm});
            skLineSegment(sketch, "E4.5.0.0", {"start": v(9.08, 395) * mm, "end": v(189.08, 395) * mm});
            skLineSegment(sketch, "E4.5.0.1", {"start": v(9.08, 480) * mm, "end": v(9.08, 395) * mm});
            skLineSegment(sketch, "E4.5.0.2", {"start": v(9.08, 480) * mm, "end": v(189.08, 480) * mm});
            skLineSegment(sketch, "E4.5.0.3", {"start": v(189.08, 480) * mm, "end": v(189.08, 395) * mm});
            skLineSegment(sketch, "E4.5.1.0", {"start": v(9.08, 270) * mm, "end": v(189.08, 270) * mm});
            skLineSegment(sketch, "E4.5.1.1", {"start": v(9.08, 355) * mm, "end": v(9.08, 270) * mm});
            skLineSegment(sketch, "E4.5.1.2", {"start": v(9.08, 355) * mm, "end": v(189.08, 355) * mm});
            skLineSegment(sketch, "E4.5.1.3", {"start": v(189.08, 355) * mm, "end": v(189.08, 270) * mm});
            skLineSegment(sketch, "E4.5.2.0", {"start": v(9.08, 145) * mm, "end": v(189.08, 145) * mm});
            skLineSegment(sketch, "E4.5.2.1", {"start": v(9.08, 230) * mm, "end": v(9.08, 145) * mm});
            skLineSegment(sketch, "E4.5.2.2", {"start": v(9.08, 230) * mm, "end": v(189.08, 230) * mm});
            skLineSegment(sketch, "E4.5.2.3", {"start": v(189.08, 230) * mm, "end": v(189.08, 145) * mm});
            skLineSegment(sketch, "E4.5.3.0", {"start": v(9.08, 20) * mm, "end": v(189.08, 20) * mm});
            skLineSegment(sketch, "E4.5.3.1", {"start": v(9.08, 105) * mm, "end": v(9.08, 20) * mm});
            skLineSegment(sketch, "E4.5.3.2", {"start": v(9.08, 105) * mm, "end": v(189.08, 105) * mm});
            skLineSegment(sketch, "E4.5.3.3", {"start": v(189.08, 105) * mm, "end": v(189.08, 20) * mm});
            skLineSegment(sketch, "E4.6.0.0", {"start": v(209.08, 395) * mm, "end": v(389.08, 395) * mm});
            skLineSegment(sketch, "E4.6.0.1", {"start": v(209.08, 480) * mm, "end": v(209.08, 395) * mm});
            skLineSegment(sketch, "E4.6.0.2", {"start": v(209.08, 480) * mm, "end": v(389.08, 480) * mm});
            skLineSegment(sketch, "E4.6.0.3", {"start": v(389.08, 480) * mm, "end": v(389.08, 395) * mm});
            skLineSegment(sketch, "E4.6.1.0", {"start": v(209.08, 270) * mm, "end": v(389.08, 270) * mm});
            skLineSegment(sketch, "E4.6.1.1", {"start": v(209.08, 355) * mm, "end": v(209.08, 270) * mm});
            skLineSegment(sketch, "E4.6.1.2", {"start": v(209.08, 355) * mm, "end": v(389.08, 355) * mm});
            skLineSegment(sketch, "E4.6.1.3", {"start": v(389.08, 355) * mm, "end": v(389.08, 270) * mm});
            skLineSegment(sketch, "E4.6.2.0", {"start": v(209.08, 145) * mm, "end": v(389.08, 145) * mm});
            skLineSegment(sketch, "E4.6.2.1", {"start": v(209.08, 230) * mm, "end": v(209.08, 145) * mm});
            skLineSegment(sketch, "E4.6.2.2", {"start": v(209.08, 230) * mm, "end": v(389.08, 230) * mm});
            skLineSegment(sketch, "E4.6.2.3", {"start": v(389.08, 230) * mm, "end": v(389.08, 145) * mm});
            skLineSegment(sketch, "E4.6.3.0", {"start": v(209.08, 20) * mm, "end": v(389.08, 20) * mm});
            skLineSegment(sketch, "E4.6.3.1", {"start": v(209.08, 105) * mm, "end": v(209.08, 20) * mm});
            skLineSegment(sketch, "E4.6.3.2", {"start": v(209.08, 105) * mm, "end": v(389.08, 105) * mm});
            skLineSegment(sketch, "E4.6.3.3", {"start": v(389.08, 105) * mm, "end": v(389.08, 20) * mm});
            skLineSegment(sketch, "E4.7.0.0", {"start": v(409.08, 395) * mm, "end": v(589.08, 395) * mm});
            skLineSegment(sketch, "E4.7.0.1", {"start": v(409.08, 480) * mm, "end": v(409.08, 395) * mm});
            skLineSegment(sketch, "E4.7.0.2", {"start": v(409.08, 480) * mm, "end": v(589.08, 480) * mm});
            skLineSegment(sketch, "E4.7.0.3", {"start": v(589.08, 480) * mm, "end": v(589.08, 395) * mm});
            skLineSegment(sketch, "E4.7.1.0", {"start": v(409.08, 270) * mm, "end": v(589.08, 270) * mm});
            skLineSegment(sketch, "E4.7.1.1", {"start": v(409.08, 355) * mm, "end": v(409.08, 270) * mm});
            skLineSegment(sketch, "E4.7.1.2", {"start": v(409.08, 355) * mm, "end": v(589.08, 355) * mm});
            skLineSegment(sketch, "E4.7.1.3", {"start": v(589.08, 355) * mm, "end": v(589.08, 270) * mm});
            skLineSegment(sketch, "E4.7.2.0", {"start": v(409.08, 145) * mm, "end": v(589.08, 145) * mm});
            skLineSegment(sketch, "E4.7.2.1", {"start": v(409.08, 230) * mm, "end": v(409.08, 145) * mm});
            skLineSegment(sketch, "E4.7.2.2", {"start": v(409.08, 230) * mm, "end": v(589.08, 230) * mm});
            skLineSegment(sketch, "E4.7.2.3", {"start": v(589.08, 230) * mm, "end": v(589.08, 145) * mm});
            skLineSegment(sketch, "E4.7.3.0", {"start": v(409.08, 20) * mm, "end": v(589.08, 20) * mm});
            skLineSegment(sketch, "E4.7.3.1", {"start": v(409.08, 105) * mm, "end": v(409.08, 20) * mm});
            skLineSegment(sketch, "E4.7.3.2", {"start": v(409.08, 105) * mm, "end": v(589.08, 105) * mm});
            skLineSegment(sketch, "E4.7.3.3", {"start": v(589.08, 105) * mm, "end": v(589.08, 20) * mm});
            skLineSegment(sketch, "E4.8.0.0", {"start": v(609.08, 395) * mm, "end": v(789.08, 395) * mm});
            skLineSegment(sketch, "E4.8.0.1", {"start": v(609.08, 480) * mm, "end": v(609.08, 395) * mm});
            skLineSegment(sketch, "E4.8.0.2", {"start": v(609.08, 480) * mm, "end": v(789.08, 480) * mm});
            skLineSegment(sketch, "E4.8.0.3", {"start": v(789.08, 480) * mm, "end": v(789.08, 395) * mm});
            skLineSegment(sketch, "E4.8.1.0", {"start": v(609.08, 270) * mm, "end": v(789.08, 270) * mm});
            skLineSegment(sketch, "E4.8.1.1", {"start": v(609.08, 355) * mm, "end": v(609.08, 270) * mm});
            skLineSegment(sketch, "E4.8.1.2", {"start": v(609.08, 355) * mm, "end": v(789.08, 355) * mm});
            skLineSegment(sketch, "E4.8.1.3", {"start": v(789.08, 355) * mm, "end": v(789.08, 270) * mm});
            skLineSegment(sketch, "E4.8.2.0", {"start": v(609.08, 145) * mm, "end": v(789.08, 145) * mm});
            skLineSegment(sketch, "E4.8.2.1", {"start": v(609.08, 230) * mm, "end": v(609.08, 145) * mm});
            skLineSegment(sketch, "E4.8.2.2", {"start": v(609.08, 230) * mm, "end": v(789.08, 230) * mm});
            skLineSegment(sketch, "E4.8.2.3", {"start": v(789.08, 230) * mm, "end": v(789.08, 145) * mm});
            skLineSegment(sketch, "E4.8.3.0", {"start": v(609.08, 20) * mm, "end": v(789.08, 20) * mm});
            skLineSegment(sketch, "E4.8.3.1", {"start": v(609.08, 105) * mm, "end": v(609.08, 20) * mm});
            skLineSegment(sketch, "E4.8.3.2", {"start": v(609.08, 105) * mm, "end": v(789.08, 105) * mm});
            skLineSegment(sketch, "E4.8.3.3", {"start": v(789.08, 105) * mm, "end": v(789.08, 20) * mm});
            skLineSegment(sketch, "E4.9.0.0", {"start": v(809.08, 395) * mm, "end": v(989.08, 395) * mm});
            skLineSegment(sketch, "E4.9.0.1", {"start": v(809.08, 480) * mm, "end": v(809.08, 395) * mm});
            skLineSegment(sketch, "E4.9.0.2", {"start": v(809.08, 480) * mm, "end": v(989.08, 480) * mm});
            skLineSegment(sketch, "E4.9.0.3", {"start": v(989.08, 480) * mm, "end": v(989.08, 395) * mm});
            skLineSegment(sketch, "E4.9.1.0", {"start": v(809.08, 270) * mm, "end": v(989.08, 270) * mm});
            skLineSegment(sketch, "E4.9.1.1", {"start": v(809.08, 355) * mm, "end": v(809.08, 270) * mm});
            skLineSegment(sketch, "E4.9.1.2", {"start": v(809.08, 355) * mm, "end": v(989.08, 355) * mm});
            skLineSegment(sketch, "E4.9.1.3", {"start": v(989.08, 355) * mm, "end": v(989.08, 270) * mm});
            skLineSegment(sketch, "E4.9.2.0", {"start": v(809.08, 145) * mm, "end": v(989.08, 145) * mm});
            skLineSegment(sketch, "E4.9.2.1", {"start": v(809.08, 230) * mm, "end": v(809.08, 145) * mm});
            skLineSegment(sketch, "E4.9.2.2", {"start": v(809.08, 230) * mm, "end": v(989.08, 230) * mm});
            skLineSegment(sketch, "E4.9.2.3", {"start": v(989.08, 230) * mm, "end": v(989.08, 145) * mm});
            skLineSegment(sketch, "E4.9.3.0", {"start": v(809.08, 20) * mm, "end": v(989.08, 20) * mm});
            skLineSegment(sketch, "E4.9.3.1", {"start": v(809.08, 105) * mm, "end": v(809.08, 20) * mm});
            skLineSegment(sketch, "E4.9.3.2", {"start": v(809.08, 105) * mm, "end": v(989.08, 105) * mm});
            skLineSegment(sketch, "E4.9.3.3", {"start": v(989.08, 105) * mm, "end": v(989.08, 20) * mm});
            skLineSegment(sketch, "E4.direction2", {"start": v(-990.92, 395) * mm, "end": v(-990.92, 270) * mm, "construction": true});
            skLineSegment(sketch, "E5.direction1", {"start": v(-990.92, 395) * mm, "end": v(-965.92, 395) * mm, "construction": true});
            skSolve(sketch);
        }
        {
            var Q0;
            Q0 = qSketchRegion(id + "F4", true);
            extrude(context, id + "F5", {"entities" : qUnion([Q0]), "operationType" : NewBodyOperationType.REMOVE, "oppositeDirection" : true, "depth" : 50 * mm});
        }
    });
